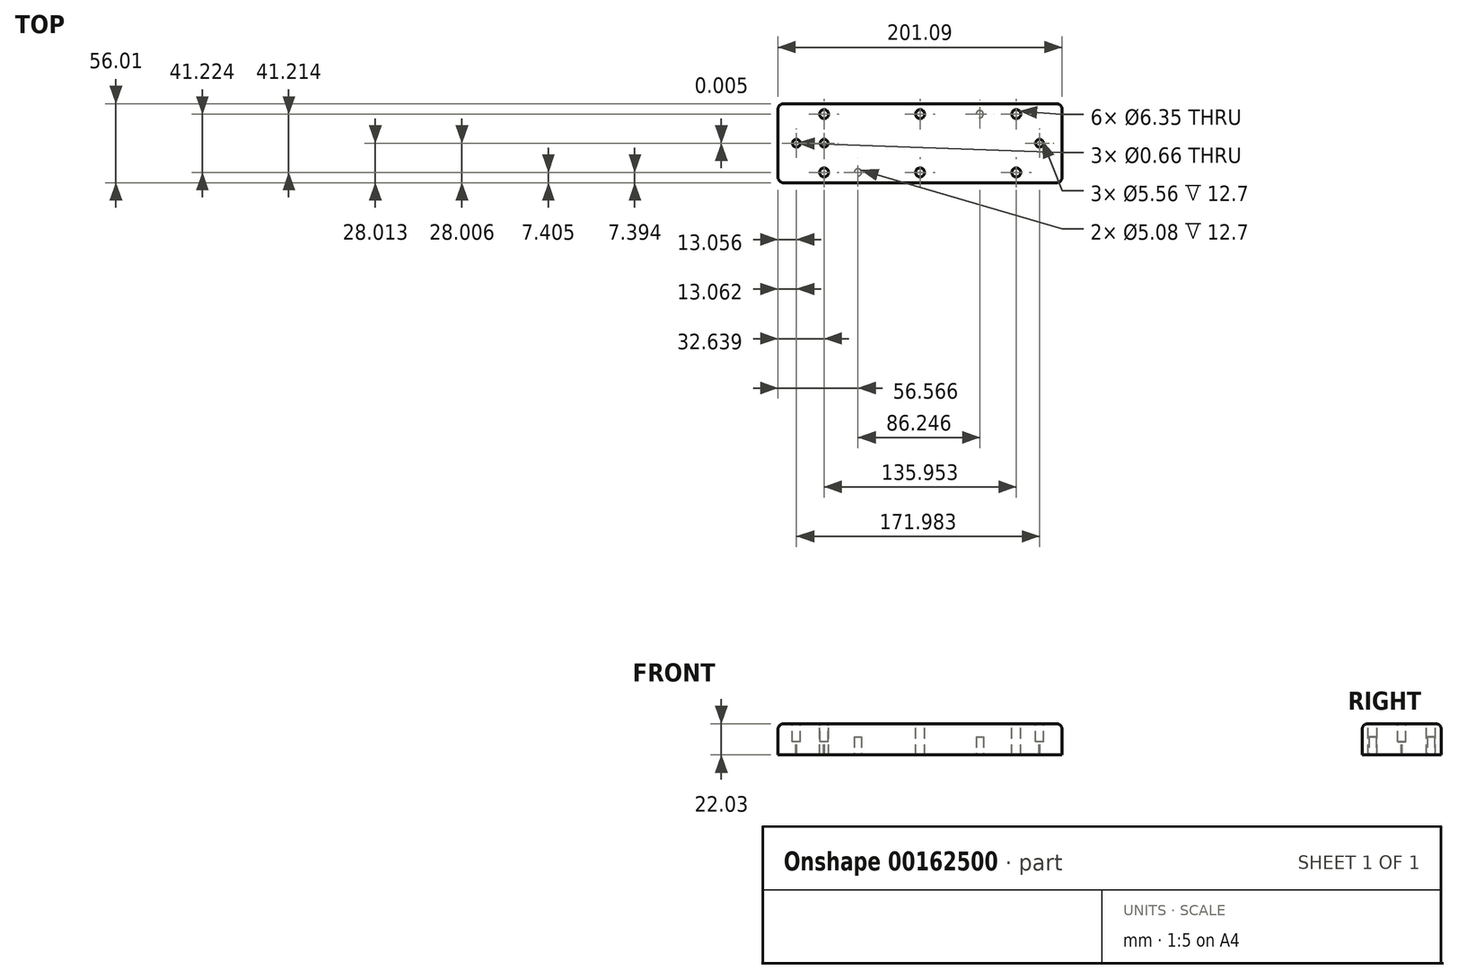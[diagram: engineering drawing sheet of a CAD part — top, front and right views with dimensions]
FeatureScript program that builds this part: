
annotation { "Feature Type Name" : "Feature", "Feature Type Description" : "" }
export const myFeature = defineFeature(function(context is Context, id is Id, definition is map)
    precondition{}
    {
        {
            var Q0;
            Q0=qCreatedBy(makeId("Top.planeOp"),FACE);
            var sketch = newSketch(context, id + "F0", { "sketchPlane" : qUnion([Q0])});
            skLineSegment(sketch, "E0.bottom", {"start": v(4.06, 0) * mm, "end": v(197.03, 0) * mm});
            skLineSegment(sketch, "E0.top", {"start": v(4.06, -56) * mm, "end": v(197.03, -56) * mm});
            skLineSegment(sketch, "E0.left", {"start": v(0, -4.06) * mm, "end": v(0, -51.94) * mm});
            skLineSegment(sketch, "E0.right", {"start": v(201.1, -4.06) * mm, "end": v(201.1, -51.94) * mm});
            skLineSegment(sketch, "E1.bottom", {"start": v(0, 0) * mm, "end": v(201.1, 0) * mm, "construction": true});
            skLineSegment(sketch, "E1.top", {"start": v(0, -7.4) * mm, "end": v(201.1, -7.4) * mm, "construction": true});
            skLineSegment(sketch, "E1.left", {"start": v(0, 0) * mm, "end": v(0, -7.4) * mm, "construction": true});
            skLineSegment(sketch, "E1.right", {"start": v(201.1, 0) * mm, "end": v(201.1, -7.4) * mm, "construction": true});
            skLineSegment(sketch, "E2.bottom", {"start": v(0, 0) * mm, "end": v(32.64, 0) * mm, "construction": true});
            skLineSegment(sketch, "E2.top", {"start": v(0, -56) * mm, "end": v(32.64, -56) * mm, "construction": true});
            skLineSegment(sketch, "E2.left", {"start": v(0, 0) * mm, "end": v(0, -56) * mm, "construction": true});
            skLineSegment(sketch, "E2.right", {"start": v(32.64, 0) * mm, "end": v(32.64, -56) * mm, "construction": true});
            skLineSegment(sketch, "E3.bottom", {"start": v(0, 0) * mm, "end": v(168.6, 0) * mm, "construction": true});
            skLineSegment(sketch, "E3.top", {"start": v(0, -56) * mm, "end": v(168.6, -56) * mm, "construction": true});
            skLineSegment(sketch, "E3.right", {"start": v(168.6, 0) * mm, "end": v(168.6, -56) * mm, "construction": true});
            skLineSegment(sketch, "E4.bottom", {"start": v(0, 0) * mm, "end": v(100.57, 0) * mm, "construction": true});
            skLineSegment(sketch, "E4.top", {"start": v(0, -56) * mm, "end": v(100.57, -56) * mm, "construction": true});
            skLineSegment(sketch, "E4.right", {"start": v(100.57, 0) * mm, "end": v(100.57, -56) * mm, "construction": true});
            skLineSegment(sketch, "E5.top", {"start": v(0, -48.6) * mm, "end": v(201.1, -48.6) * mm, "construction": true});
            skLineSegment(sketch, "E5.left", {"start": v(0, 0) * mm, "end": v(0, -48.6) * mm, "construction": true});
            skLineSegment(sketch, "E5.right", {"start": v(201.1, 0) * mm, "end": v(201.1, -48.6) * mm, "construction": true});
            skLineSegment(sketch, "E6.bottom", {"start": v(0, 0) * mm, "end": v(52.5, 0) * mm, "construction": true});
            skLineSegment(sketch, "E6.top", {"start": v(0, -56) * mm, "end": v(52.5, -56) * mm, "construction": true});
            skLineSegment(sketch, "E6.right", {"start": v(52.5, 0) * mm, "end": v(52.5, -56) * mm, "construction": true});
            skCircle(sketch, "E7", {"center": v(32.64, -7.4) * mm, "radius": 3.18 * mm});
            skCircle(sketch, "E8", {"center": v(100.57, -7.4) * mm, "radius": 3.18 * mm});
            skCircle(sketch, "E9", {"center": v(168.6, -7.4) * mm, "radius": 3.18 * mm});
            skCircle(sketch, "E10", {"center": v(168.6, -48.6) * mm, "radius": 3.18 * mm});
            skCircle(sketch, "E11", {"center": v(100.55, -48.6) * mm, "radius": 3.18 * mm});
            skCircle(sketch, "E12", {"center": v(32.64, -48.6) * mm, "radius": 3.18 * mm});
            skLineSegment(sketch, "E13.bottom", {"start": v(0, 0) * mm, "end": v(138.75, 0) * mm, "construction": true});
            skLineSegment(sketch, "E13.top", {"start": v(0, -56) * mm, "end": v(138.75, -56) * mm, "construction": true});
            skLineSegment(sketch, "E13.right", {"start": v(138.75, 0) * mm, "end": v(138.75, -56) * mm, "construction": true});
            skLineSegment(sketch, "E14.top", {"start": v(0, -56) * mm, "end": v(201.1, -56) * mm, "construction": true});
            skLineSegment(sketch, "E14.right", {"start": v(201.1, 0) * mm, "end": v(201.1, -56) * mm, "construction": true});
            skPoint(sketch, "E15.visualSharp", {"position": v(201.1, 0) * mm});
            skArc(sketch, "E15.filletArc", {"start": v(201.1, -4.06) * mm, "mid": v(199.9, -1.2) * mm, "end": v(197.03, 0) * mm});
            skPoint(sketch, "E16.visualSharp", {"position": v(0, -56) * mm});
            skArc(sketch, "E16.filletArc", {"start": v(0, -51.94) * mm, "mid": v(1.2, -54.82) * mm, "end": v(4.06, -56) * mm});
            skPoint(sketch, "E17.visualSharp", {"position": v(201.1, -56) * mm});
            skArc(sketch, "E17.filletArc", {"start": v(197.03, -56) * mm, "mid": v(199.9, -54.82) * mm, "end": v(201.1, -51.94) * mm});
            skPoint(sketch, "E18.visualSharp", {"position": v(0, 0) * mm});
            skArc(sketch, "E18.filletArc", {"start": v(4.06, 0) * mm, "mid": v(1.2, -1.2) * mm, "end": v(0, -4.06) * mm});
            skSolve(sketch);
        }
        {
            var Q0;
            Q0 = qSketchRegion(id + "F0", true);
            extrude(context, id + "F1", {"entities" : qUnion([Q0]), "oppositeDirection" : true, "depth" : 22.03 * mm});
        }
        {
            var Q0;
            Q0=makeQuery(id+"F1.opExtrude","CAP_FACE",FACE,{"disambiguationData":[OSD([sQuery(id+"F0.wireOp",EDGE,"E0.bottom"),sQuery(id+"F0.wireOp",EDGE,"E0.top"),sQuery(id+"F0.wireOp",EDGE,"E0.left"),sQuery(id+"F0.wireOp",EDGE,"E0.right"),sQuery(id+"F0.wireOp",EDGE,"E7"),sQuery(id+"F0.wireOp",EDGE,"E8"),sQuery(id+"F0.wireOp",EDGE,"E9"),sQuery(id+"F0.wireOp",EDGE,"E10"),sQuery(id+"F0.wireOp",EDGE,"E11"),sQuery(id+"F0.wireOp",EDGE,"E12")])],"isStart":false});
            var sketch = newSketch(context, id + "F2", { "sketchPlane" : qUnion([Q0])});
            skLineSegment(sketch, "E19.bottom", {"start": v(4.06, 0) * mm, "end": v(201.1, 0) * mm, "construction": true});
            skLineSegment(sketch, "E19.top", {"start": v(4.06, 7.4) * mm, "end": v(201.1, 7.4) * mm, "construction": true});
            skLineSegment(sketch, "E19.left", {"start": v(4.06, 0) * mm, "end": v(4.06, 7.4) * mm, "construction": true});
            skLineSegment(sketch, "E19.right", {"start": v(201.1, 0) * mm, "end": v(201.1, 7.4) * mm, "construction": true});
            skLineSegment(sketch, "E20.top", {"start": v(4.06, 48.62) * mm, "end": v(201.1, 48.62) * mm, "construction": true});
            skLineSegment(sketch, "E20.left", {"start": v(4.06, 0) * mm, "end": v(4.06, 48.62) * mm, "construction": true});
            skLineSegment(sketch, "E20.right", {"start": v(201.1, 0) * mm, "end": v(201.1, 48.62) * mm, "construction": true});
            skLineSegment(sketch, "E21.bottom", {"start": v(4.06, 0) * mm, "end": v(56.57, 0) * mm, "construction": true});
            skLineSegment(sketch, "E21.top", {"start": v(4.06, 56) * mm, "end": v(56.57, 56) * mm, "construction": true});
            skLineSegment(sketch, "E21.left", {"start": v(4.06, 0) * mm, "end": v(4.06, 56) * mm, "construction": true});
            skLineSegment(sketch, "E21.right", {"start": v(56.57, 0) * mm, "end": v(56.57, 56) * mm, "construction": true});
            skLineSegment(sketch, "E22.bottom", {"start": v(4.06, 0) * mm, "end": v(142.81, 0) * mm, "construction": true});
            skLineSegment(sketch, "E22.top", {"start": v(4.06, 56) * mm, "end": v(142.81, 56) * mm, "construction": true});
            skLineSegment(sketch, "E22.right", {"start": v(142.81, 0) * mm, "end": v(142.81, 56) * mm, "construction": true});
            skCircle(sketch, "E23", {"center": v(56.57, 48.62) * mm, "radius": 2.54 * mm});
            skCircle(sketch, "E24", {"center": v(142.81, 7.4) * mm, "radius": 2.54 * mm});
            skSolve(sketch);
        }
        {
            var Q0;
            Q0 = qSketchRegion(id + "F2", true);
            extrude(context, id + "F3", {"entities" : qUnion([Q0]), "operationType" : NewBodyOperationType.REMOVE, "oppositeDirection" : true, "depth" : 12.7 * mm});
        }
        {
            var Q0;
            Q0=makeQuery(id+"F1.opExtrude","CAP_FACE",FACE,{"disambiguationData":[OSD([sQuery(id+"F0.wireOp",EDGE,"E0.bottom"),sQuery(id+"F0.wireOp",EDGE,"E0.top"),sQuery(id+"F0.wireOp",EDGE,"E0.left"),sQuery(id+"F0.wireOp",EDGE,"E0.right"),sQuery(id+"F0.wireOp",EDGE,"E7"),sQuery(id+"F0.wireOp",EDGE,"E8"),sQuery(id+"F0.wireOp",EDGE,"E9"),sQuery(id+"F0.wireOp",EDGE,"E10"),sQuery(id+"F0.wireOp",EDGE,"E11"),sQuery(id+"F0.wireOp",EDGE,"E12")])],"isStart":true});
            var sketch = newSketch(context, id + "F4", { "sketchPlane" : qUnion([Q0])});
            skLineSegment(sketch, "E25.bottom", {"start": v(0, 0) * mm, "end": v(201.1, 0) * mm, "construction": true});
            skLineSegment(sketch, "E25.top", {"start": v(0, -28) * mm, "end": v(201.1, -28) * mm, "construction": true});
            skLineSegment(sketch, "E25.left", {"start": v(0, 0) * mm, "end": v(0, -28) * mm, "construction": true});
            skLineSegment(sketch, "E25.right", {"start": v(201.1, 0) * mm, "end": v(201.1, -28) * mm, "construction": true});
            skLineSegment(sketch, "E26.bottom", {"start": v(0, 0) * mm, "end": v(13.06, 0) * mm, "construction": true});
            skLineSegment(sketch, "E26.top", {"start": v(0, -56) * mm, "end": v(13.06, -56) * mm, "construction": true});
            skLineSegment(sketch, "E26.left", {"start": v(0, 0) * mm, "end": v(0, -56) * mm, "construction": true});
            skLineSegment(sketch, "E26.right", {"start": v(13.06, 0) * mm, "end": v(13.06, -56) * mm, "construction": true});
            skLineSegment(sketch, "E27.bottom", {"start": v(0, 0) * mm, "end": v(32.69, 0) * mm, "construction": true});
            skLineSegment(sketch, "E27.top", {"start": v(0, -56) * mm, "end": v(32.69, -56) * mm, "construction": true});
            skLineSegment(sketch, "E27.right", {"start": v(32.69, 0) * mm, "end": v(32.69, -56) * mm, "construction": true});
            skLineSegment(sketch, "E28.bottom", {"start": v(0, 0) * mm, "end": v(185.04, 0) * mm, "construction": true});
            skLineSegment(sketch, "E28.top", {"start": v(0, -56) * mm, "end": v(185.04, -56) * mm, "construction": true});
            skLineSegment(sketch, "E28.right", {"start": v(185.04, 0) * mm, "end": v(185.04, -56) * mm, "construction": true});
            skCircle(sketch, "E29", {"center": v(32.69, -28) * mm, "radius": 0.33 * mm});
            skCircle(sketch, "E30", {"center": v(13.06, -28) * mm, "radius": 0.33 * mm});
            skCircle(sketch, "E31", {"center": v(185.04, -28) * mm, "radius": 0.33 * mm});
            skSolve(sketch);
        }
        {
            var Q0;
            Q0 = qSketchRegion(id + "F4", true);
            extrude(context, id + "F5", {"entities" : qUnion([Q0]), "operationType" : NewBodyOperationType.REMOVE, "oppositeDirection" : true, "depth" : 25.4 * mm});
        }
        {
            var Q0;
            Q0=qCreatedBy(makeId("Top.planeOp"),FACE);
            var sketch = newSketch(context, id + "F6", { "sketchPlane" : qUnion([Q0])});
            skLineSegment(sketch, "E32.bottom", {"start": v(0, 0) * mm, "end": v(201.1, 0) * mm, "construction": true});
            skLineSegment(sketch, "E32.top", {"start": v(0, -28) * mm, "end": v(201.1, -28) * mm, "construction": true});
            skLineSegment(sketch, "E32.left", {"start": v(0, 0) * mm, "end": v(0, -28) * mm, "construction": true});
            skLineSegment(sketch, "E32.right", {"start": v(201.1, 0) * mm, "end": v(201.1, -28) * mm, "construction": true});
            skLineSegment(sketch, "E33.bottom", {"start": v(0, 0) * mm, "end": v(13.06, 0) * mm, "construction": true});
            skLineSegment(sketch, "E33.top", {"start": v(0, -56) * mm, "end": v(13.06, -56) * mm, "construction": true});
            skLineSegment(sketch, "E33.left", {"start": v(0, 0) * mm, "end": v(0, -56) * mm, "construction": true});
            skLineSegment(sketch, "E33.right", {"start": v(13.06, 0) * mm, "end": v(13.06, -56) * mm, "construction": true});
            skLineSegment(sketch, "E34.bottom", {"start": v(0, 0) * mm, "end": v(32.7, 0) * mm, "construction": true});
            skLineSegment(sketch, "E34.top", {"start": v(0, -56) * mm, "end": v(32.7, -56) * mm, "construction": true});
            skLineSegment(sketch, "E34.right", {"start": v(32.7, 0) * mm, "end": v(32.7, -56) * mm, "construction": true});
            skLineSegment(sketch, "E35.bottom", {"start": v(0, 0) * mm, "end": v(185.05, 0) * mm, "construction": true});
            skLineSegment(sketch, "E35.top", {"start": v(0, -56) * mm, "end": v(185.05, -56) * mm, "construction": true});
            skLineSegment(sketch, "E35.right", {"start": v(185.05, 0) * mm, "end": v(185.05, -56) * mm, "construction": true});
            skCircle(sketch, "E36", {"center": v(185.05, -28) * mm, "radius": 2.78 * mm});
            skCircle(sketch, "E37", {"center": v(32.7, -28) * mm, "radius": 2.78 * mm});
            skCircle(sketch, "E38", {"center": v(13.06, -28) * mm, "radius": 2.78 * mm});
            skSolve(sketch);
        }
        {
            var Q0;
            Q0 = qSketchRegion(id + "F6", true);
            extrude(context, id + "F7", {"entities" : qUnion([Q0]), "operationType" : NewBodyOperationType.REMOVE, "oppositeDirection" : true, "depth" : 12.7 * mm});
        }
        {
            var Q0;
            Q0=makeQuery(id+"F1.opExtrude","CAP_FACE",FACE,{"disambiguationData":[OSD([sQuery(id+"F0.wireOp",EDGE,"E0.bottom"),sQuery(id+"F0.wireOp",EDGE,"E0.top"),sQuery(id+"F0.wireOp",EDGE,"E0.left"),sQuery(id+"F0.wireOp",EDGE,"E0.right"),sQuery(id+"F0.wireOp",EDGE,"E7"),sQuery(id+"F0.wireOp",EDGE,"E8"),sQuery(id+"F0.wireOp",EDGE,"E9"),sQuery(id+"F0.wireOp",EDGE,"E10"),sQuery(id+"F0.wireOp",EDGE,"E11"),sQuery(id+"F0.wireOp",EDGE,"E12")])],"isStart":false});
            var sketch = newSketch(context, id + "F8", { "sketchPlane" : qUnion([Q0])});
            skLineSegment(sketch, "E39.bottom", {"start": v(4.06, 0) * mm, "end": v(201.1, 0) * mm, "construction": true});
            skLineSegment(sketch, "E39.top", {"start": v(4.06, 28) * mm, "end": v(201.1, 28) * mm, "construction": true});
            skLineSegment(sketch, "E39.left", {"start": v(4.06, 0) * mm, "end": v(4.06, 28) * mm, "construction": true});
            skLineSegment(sketch, "E39.right", {"start": v(201.1, 0) * mm, "end": v(201.1, 28) * mm, "construction": true});
            skLineSegment(sketch, "E40.bottom", {"start": v(4.06, 0) * mm, "end": v(32.48, 0) * mm, "construction": true});
            skLineSegment(sketch, "E40.top", {"start": v(4.06, 56) * mm, "end": v(32.48, 56) * mm, "construction": true});
            skLineSegment(sketch, "E40.left", {"start": v(4.06, 0) * mm, "end": v(4.06, 56) * mm, "construction": true});
            skLineSegment(sketch, "E40.right", {"start": v(32.48, 0) * mm, "end": v(32.48, 56) * mm, "construction": true});
            skLineSegment(sketch, "E41.bottom", {"start": v(4.06, 0) * mm, "end": v(185.55, 0) * mm});
            skLineSegment(sketch, "E41.top", {"start": v(4.06, 56) * mm, "end": v(185.55, 56) * mm, "construction": true});
            skLineSegment(sketch, "E41.left", {"start": v(4.06, 0) * mm, "end": v(4.06, 56) * mm});
            skLineSegment(sketch, "E42.bottom", {"start": v(4.06, 0) * mm, "end": v(12.8, 0) * mm, "construction": true});
            skLineSegment(sketch, "E42.top", {"start": v(4.06, 56) * mm, "end": v(12.8, 56) * mm, "construction": true});
            skLineSegment(sketch, "E43.bottom", {"start": v(4.06, 0) * mm, "end": v(131.06, 0) * mm, "construction": true});
            skLineSegment(sketch, "E43.top", {"start": v(4.06, 17.27) * mm, "end": v(131.06, 17.27) * mm, "construction": true});
            skLineSegment(sketch, "E43.left", {"start": v(4.06, 0) * mm, "end": v(4.06, 17.27) * mm, "construction": true});
            skLineSegment(sketch, "E43.right", {"start": v(131.06, 0) * mm, "end": v(131.06, 17.27) * mm, "construction": true});
            skLineSegment(sketch, "E44.bottom", {"start": v(4.06, 0) * mm, "end": v(156.46, 0) * mm, "construction": true});
            skLineSegment(sketch, "E44.top", {"start": v(4.06, 38.73) * mm, "end": v(156.46, 38.73) * mm, "construction": true});
            skLineSegment(sketch, "E44.left", {"start": v(4.06, 0) * mm, "end": v(4.06, 38.73) * mm, "construction": true});
            skLineSegment(sketch, "E44.right", {"start": v(156.46, 0) * mm, "end": v(156.46, 38.73) * mm, "construction": true});
            skLineSegment(sketch, "E45", {"start": v(32.36, 28) * mm, "end": v(32.36, 28) * mm});
            skLineSegment(sketch, "E46", {"start": v(32.48, 17.27) * mm, "end": v(12.9, 27.7) * mm});
            skLineSegment(sketch, "E47", {"start": v(12.9, 27.7) * mm, "end": v(12.9, 28.29) * mm});
            skLineSegment(sketch, "E48", {"start": v(12.9, 28.29) * mm, "end": v(32.48, 38.73) * mm});
            skLineSegment(sketch, "E49", {"start": v(32.48, 38.73) * mm, "end": v(185.06, 28.33) * mm});
            skLineSegment(sketch, "E50", {"start": v(185.06, 28.33) * mm, "end": v(185.06, 27.67) * mm});
            skLineSegment(sketch, "E51", {"start": v(185.06, 27.67) * mm, "end": v(32.48, 17.27) * mm});
            skSolve(sketch);
        }
        {
            var Q0;
            Q0=makeQuery(id+"F1.opExtrude","CAP_EDGE",EDGE,{"disambiguationData":[OSD([sQuery(id+"F0.wireOp",EDGE,"E0.top")])],"isStart":true});
            var Q1;
            Q1=makeQuery(id+"F1.opExtrude","CAP_EDGE",EDGE,{"disambiguationData":[OSD([sQuery(id+"F0.wireOp",EDGE,"E17.filletArc")])],"isStart":true});
            var Q2;
            Q2=makeQuery(id+"F1.opExtrude","CAP_EDGE",EDGE,{"disambiguationData":[OSD([sQuery(id+"F0.wireOp",EDGE,"E0.right")])],"isStart":true});
            var Q3;
            Q3=makeQuery(id+"F1.opExtrude","CAP_EDGE",EDGE,{"disambiguationData":[OSD([sQuery(id+"F0.wireOp",EDGE,"E15.filletArc")])],"isStart":true});
            var Q4;
            Q4=makeQuery(id+"F1.opExtrude","CAP_EDGE",EDGE,{"disambiguationData":[OSD([sQuery(id+"F0.wireOp",EDGE,"E0.bottom")])],"isStart":true});
            var Q5;
            Q5=makeQuery(id+"F1.opExtrude","CAP_EDGE",EDGE,{"disambiguationData":[OSD([sQuery(id+"F0.wireOp",EDGE,"E18.filletArc")])],"isStart":true});
            var Q6;
            Q6=makeQuery(id+"F1.opExtrude","CAP_EDGE",EDGE,{"disambiguationData":[OSD([sQuery(id+"F0.wireOp",EDGE,"E0.left")])],"isStart":true});
            var Q7;
            Q7=makeQuery(id+"F1.opExtrude","CAP_EDGE",EDGE,{"disambiguationData":[OSD([sQuery(id+"F0.wireOp",EDGE,"E16.filletArc")])],"isStart":true});
            fillet(context, id + "F9", {"entities" : qUnion([Q0, Q1, Q2, Q3, Q4, Q5, Q6, Q7]), "radius" : 4.06 * mm, "tangentPropagation" : true, "allowEdgeOverflow" : false});
        }
    });
